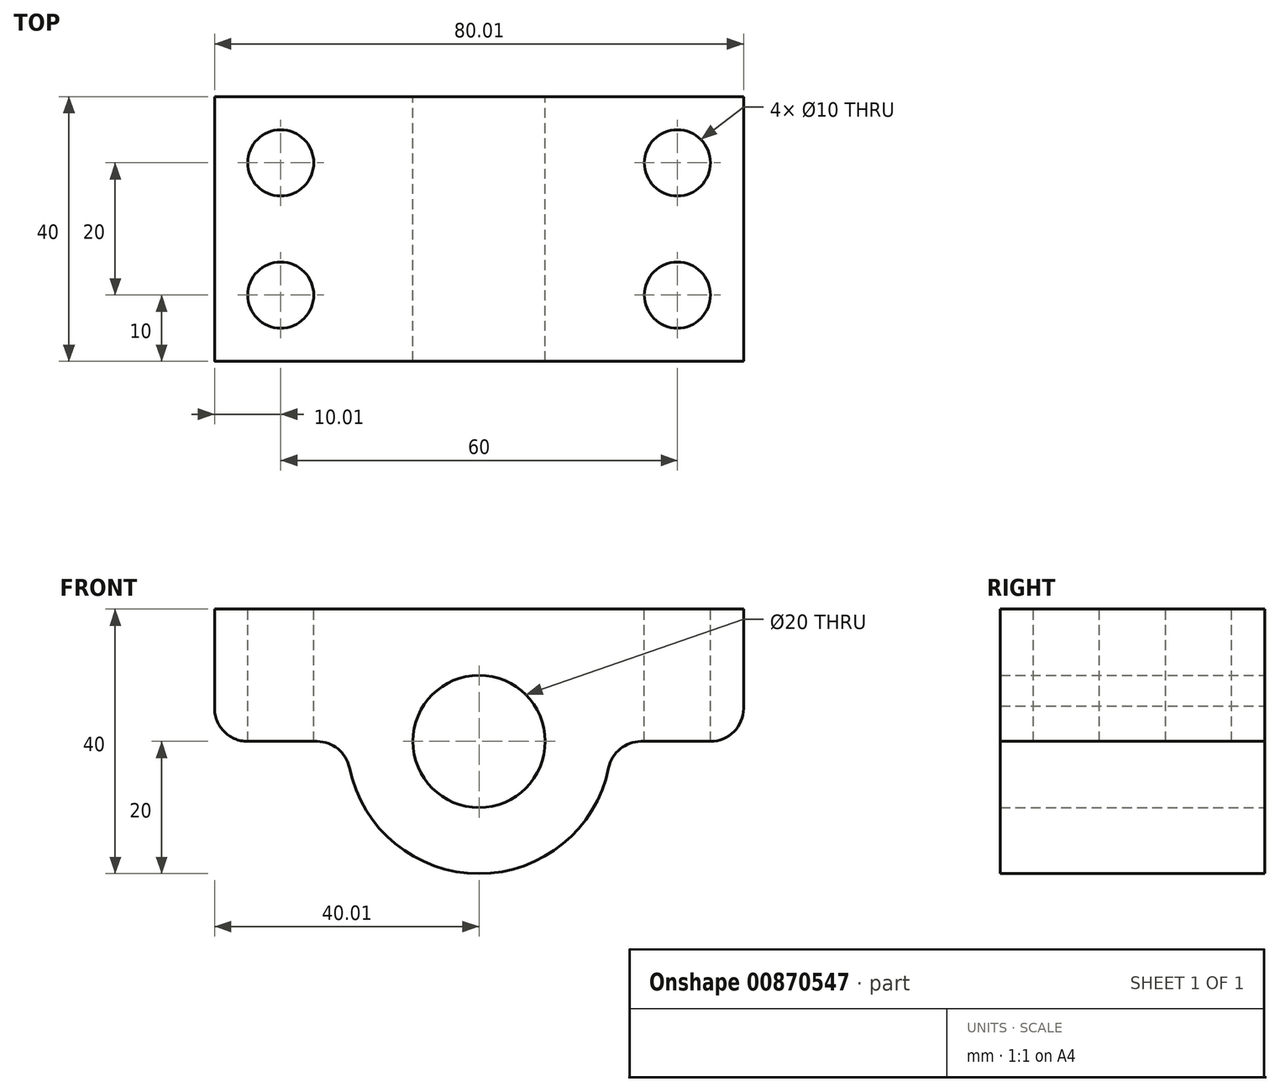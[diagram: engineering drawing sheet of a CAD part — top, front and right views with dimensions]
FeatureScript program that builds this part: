
annotation { "Feature Type Name" : "Feature", "Feature Type Description" : "" }
export const myFeature = defineFeature(function(context is Context, id is Id, definition is map)
    precondition{}
    {
        {
            var Q0;
            Q0=qCreatedBy(makeId("Front.planeOp"),FACE);
            var sketch = newSketch(context, id + "F0", { "sketchPlane" : qUnion([Q0])});
            skCircle(sketch, "E0", {"center": v(0, 0) * mm, "radius": 10 * mm});
            skArc(sketch, "E1", {"start": v(-19.6, -4) * mm, "mid": v(0, -20) * mm, "end": v(19.6, -4) * mm});
            skLineSegment(sketch, "E2.bottom", {"start": v(24.5, 0) * mm, "end": v(35, 0) * mm});
            skPoint(sketch, "E3.newPointB", {"position": v(-40, 0) * mm});
            skArc(sketch, "E3.filletArc", {"start": v(24.5, 0) * mm, "mid": v(21.33, -1.13) * mm, "end": v(19.6, -4) * mm});
            skPoint(sketch, "E4.visualSharp", {"position": v(40, 0) * mm});
            skArc(sketch, "E4.filletArc", {"start": v(35, 0) * mm, "mid": v(38.54, 1.46) * mm, "end": v(40, 5) * mm});
            skLineSegment(sketch, "E5", {"start": v(-35.01, 0) * mm, "end": v(-24.5, 0) * mm});
            skPoint(sketch, "E6.visualSharp", {"position": v(-20, 0) * mm});
            skArc(sketch, "E6.filletArc", {"start": v(-19.6, -4) * mm, "mid": v(-21.33, -1.13) * mm, "end": v(-24.5, 0) * mm});
            skArc(sketch, "E7.filletArc", {"start": v(-40, 5.34) * mm, "mid": v(-38.67, 1.59) * mm, "end": v(-35.01, 0) * mm});
            skPoint(sketch, "E8.visualSharp", {"position": v(40, 20) * mm});
            skLineSegment(sketch, "E9", {"start": v(40, 5) * mm, "end": v(40, 20) * mm});
            skLineSegment(sketch, "E10", {"start": v(-40, 5.34) * mm, "end": v(-40, 20) * mm});
            skLineSegment(sketch, "E11", {"start": v(-40, 20) * mm, "end": v(40, 20) * mm});
            skSolve(sketch);
        }
        {
            var Q0;
            Q0 = qSketchRegion(id + "F0", true);
            var Q1;
            Q1 = qSketchRegion(id + "FllacKS9d2WpJD6_0", true);
            extrude(context, id + "F1", {"entities" : qUnion([Q0, Q1]), "depth" : 40 * mm, "offsetDistance" : 25 * mm});
        }
        {
            var Q0;
            Q0=makeQuery(id+"F1.opExtrude","SWEPT_FACE",FACE,{"disambiguationData":[OSD([sQuery(id+"F0.wireOp",EDGE,"E11")])]});
            var sketch = newSketch(context, id + "F2", { "sketchPlane" : qUnion([Q0])});
            skPoint(sketch, "E12", {"position": v(-30, -10) * mm});
            skPoint(sketch, "E13", {"position": v(-30, -30) * mm});
            skPoint(sketch, "E14", {"position": v(30, -30) * mm});
            skPoint(sketch, "E15", {"position": v(30, -10) * mm});
            skSolve(sketch);
        }
        {
            var Q0;
            Q0=sQuery(id+"F2.wireOp",VERTEX,"E12");
            var Q1;
            Q1=sQuery(id+"F2.wireOp",VERTEX,"E13");
            var Q2;
            Q2=sQuery(id+"F2.wireOp",VERTEX,"E14");
            var Q3;
            Q3=sQuery(id+"F2.wireOp",VERTEX,"E15");
            var Q4;
            Q4=makeQuery(id+"F1.opExtrude","SWEPT_BODY",BODY,{"disambiguationData":[OSD([sQuery(id+"F0.wireOp",EDGE,"E0"),sQuery(id+"F0.wireOp",EDGE,"E1"),sQuery(id+"F0.wireOp",EDGE,"E2.bottom"),sQuery(id+"F0.wireOp",EDGE,"E3.filletArc"),sQuery(id+"F0.wireOp",EDGE,"E4.filletArc"),sQuery(id+"F0.wireOp",EDGE,"E5"),sQuery(id+"F0.wireOp",EDGE,"E6.filletArc"),sQuery(id+"F0.wireOp",EDGE,"E7.filletArc"),sQuery(id+"F0.wireOp",EDGE,"E9"),sQuery(id+"F0.wireOp",EDGE,"E10"),sQuery(id+"F0.wireOp",EDGE,"E11")])]});
            hole(context, id + "F3", {"style" : HoleStyle.SIMPLE, "endStyle" : HoleEndStyle.THROUGH, "holeDiameter" : 10 * mm, "majorDiameter" : 5 * mm, "isTappedThrough" : true, "tappedDepth" : 12 * mm, "tapClearance" : 3, "locations" : qUnion([Q0, Q1, Q2, Q3]), "scope" : qUnion([Q4])});
        }
    });
